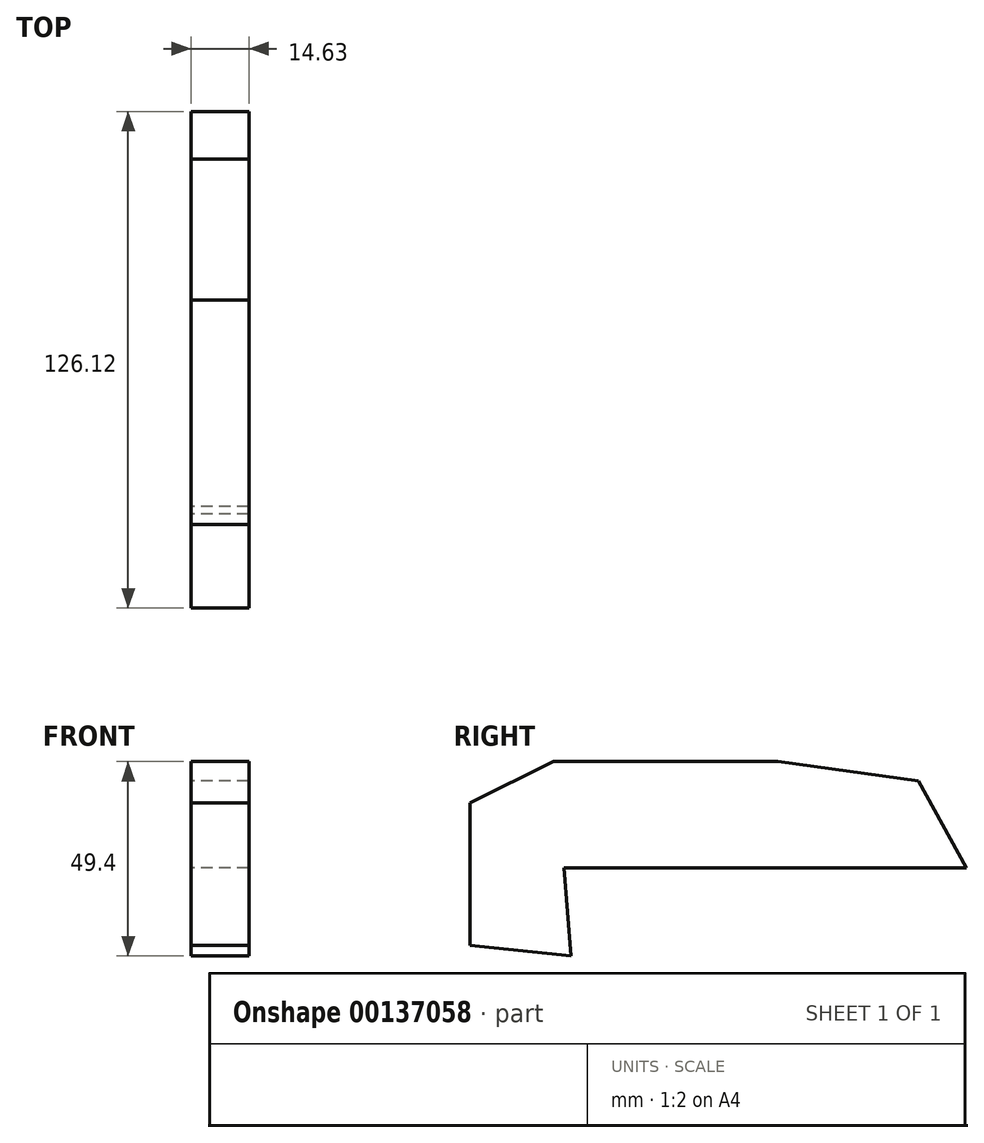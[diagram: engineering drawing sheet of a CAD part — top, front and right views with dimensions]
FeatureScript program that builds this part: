
annotation { "Feature Type Name" : "Feature", "Feature Type Description" : "" }
export const myFeature = defineFeature(function(context is Context, id is Id, definition is map)
    precondition{}
    {
        {
            var Q0;
            Q0=qCreatedBy(makeId("Right.planeOp"),FACE);
            var sketch = newSketch(context, id + "F0", { "sketchPlane" : qUnion([Q0])});
            skLineSegment(sketch, "E0", {"start": v(-55.18, -13) * mm, "end": v(-55.18, 23.25) * mm});
            skLineSegment(sketch, "E1", {"start": v(-55.18, 23.25) * mm, "end": v(-33.9, 33.76) * mm});
            skLineSegment(sketch, "E2", {"start": v(-33.9, 33.76) * mm, "end": v(23.12, 33.76) * mm});
            skLineSegment(sketch, "E3", {"start": v(23.12, 33.76) * mm, "end": v(58.86, 28.77) * mm});
            skLineSegment(sketch, "E4", {"start": v(58.86, 28.77) * mm, "end": v(70.94, 6.7) * mm});
            skLineSegment(sketch, "E5", {"start": v(70.94, 6.7) * mm, "end": v(0, 6.7) * mm});
            skLineSegment(sketch, "E6", {"start": v(0, 6.7) * mm, "end": v(-31.27, 6.7) * mm});
            skLineSegment(sketch, "E7", {"start": v(-31.27, 6.7) * mm, "end": v(-29.43, -15.64) * mm});
            skLineSegment(sketch, "E8", {"start": v(-29.43, -15.64) * mm, "end": v(-55.18, -13) * mm});
            skSolve(sketch);
        }
        {
            var Q0;
            Q0=makeQuery(id+"F0.imprint","IMPRINT",FACE,{"disambiguationData":[TD([[makeQuery(id+"F0.imprint","IMPRINT",EDGE,{"derivedFrom":sQuery(id+"F0.wireOp",EDGE,"E0")}),-1.0]])]});
            var Q1;
            Q1=sQuery(id+"F0.wireOp",EDGE,"E7");
            var Q2;
            Q2=sQuery(id+"F0.wireOp",EDGE,"E1");
            var Q3;
            Q3=sQuery(id+"F0.wireOp",EDGE,"E6");
            var Q4;
            Q4=sQuery(id+"F0.wireOp",EDGE,"E3");
            var Q5;
            Q5=sQuery(id+"F0.wireOp",EDGE,"E2");
            var Q6;
            Q6=sQuery(id+"F0.wireOp",EDGE,"E5");
            var Q7;
            Q7=sQuery(id+"F0.wireOp",EDGE,"E8");
            var Q8;
            Q8=sQuery(id+"F0.wireOp",EDGE,"E4");
            var Q9;
            Q9=sQuery(id+"F0.wireOp",EDGE,"E0");
            extrude(context, id + "F1", {"entities" : qUnion([Q0]), "surfaceEntities" : qUnion([Q1, Q2, Q3, Q4, Q5, Q6, Q7, Q8, Q9]), "depth" : 14.63 * mm});
        }
    });
